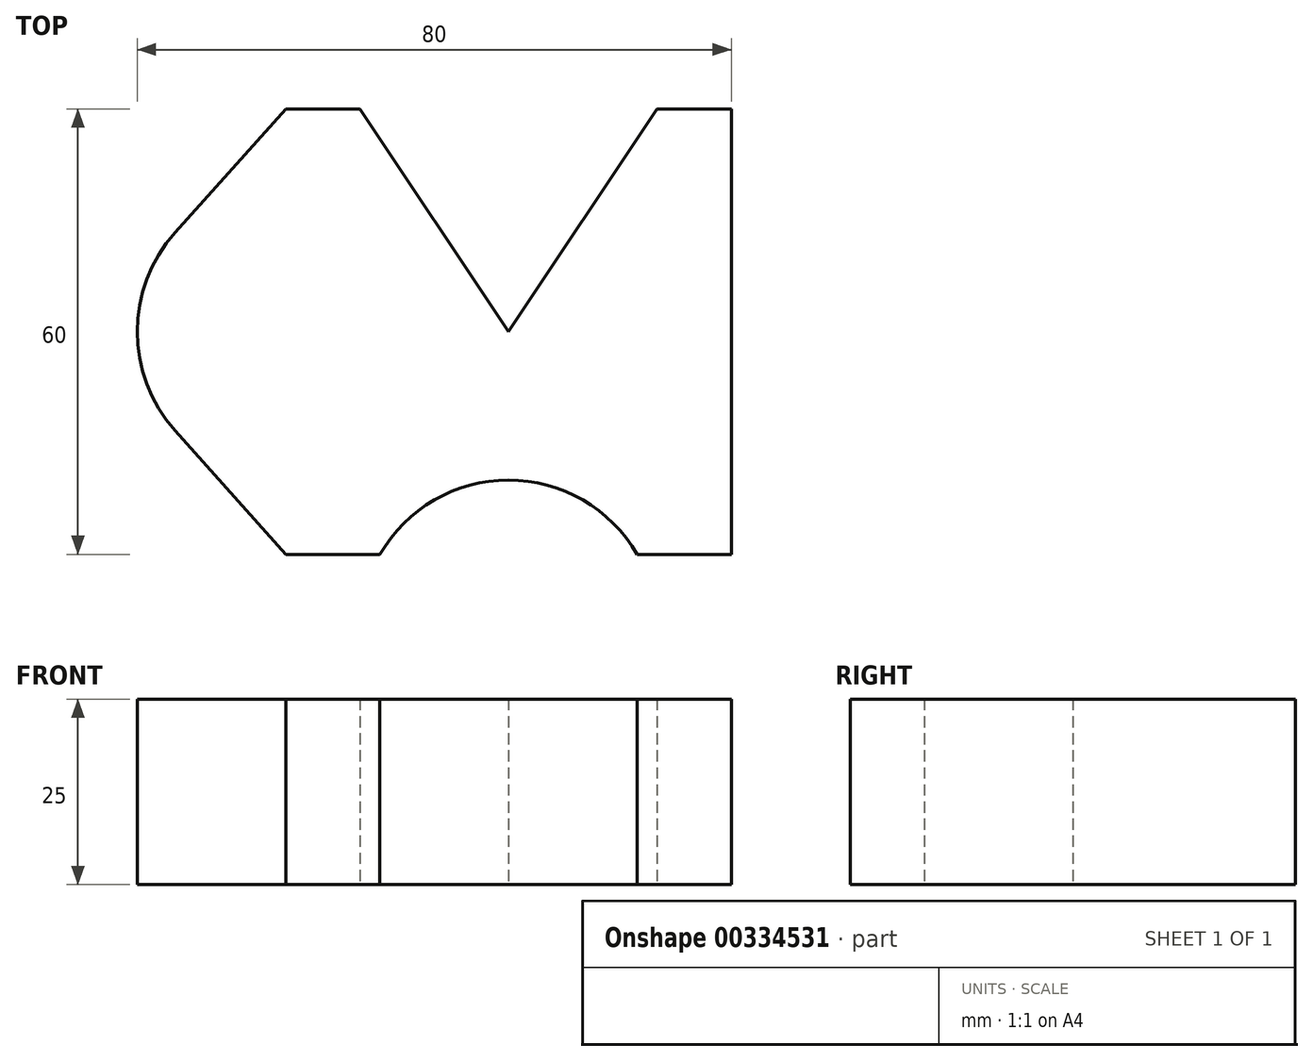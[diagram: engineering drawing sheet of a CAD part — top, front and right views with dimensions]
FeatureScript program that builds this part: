
annotation { "Feature Type Name" : "Feature", "Feature Type Description" : "" }
export const myFeature = defineFeature(function(context is Context, id is Id, definition is map)
    precondition{}
    {
        {
            var Q0;
            Q0=qCreatedBy(makeId("Top.planeOp"),FACE);
            var sketch = newSketch(context, id + "F0", { "sketchPlane" : qUnion([Q0])});
            skLineSegment(sketch, "E0", {"start": v(0, 0) * mm, "end": v(20, 30) * mm});
            skLineSegment(sketch, "E1", {"start": v(20, 30) * mm, "end": v(30, 30) * mm});
            skLineSegment(sketch, "E2", {"start": v(30, 30) * mm, "end": v(30, -30) * mm});
            skLineSegment(sketch, "E3", {"start": v(30, -30) * mm, "end": v(-19.9, -30) * mm});
            skCircle(sketch, "E4", {"center": v(-30, 0) * mm, "radius": 20 * mm});
            skCircle(sketch, "E5", {"center": v(0, -40) * mm, "radius": 20 * mm});
            skLineSegment(sketch, "E6", {"start": v(0, 0) * mm, "end": v(-20, 30) * mm});
            skLineSegment(sketch, "E7", {"start": v(-20, 30) * mm, "end": v(-30, 30) * mm});
            skLineSegment(sketch, "E8", {"start": v(-30, 30) * mm, "end": v(-44.9, 13.33) * mm});
            skLineSegment(sketch, "E9", {"start": v(-19.9, -30) * mm, "end": v(-30, -30) * mm});
            skLineSegment(sketch, "E10", {"start": v(-30, -30) * mm, "end": v(-44.9, -13.33) * mm});
            skSolve(sketch);
        }
        {
            var Q0;
            Q0=makeQuery(id+"F0.imprint","IMPRINT",FACE,{"disambiguationData":[TD([[makeQuery(id+"F0.imprint","IMPRINT",EDGE,{"derivedFrom":sQuery(id+"F0.wireOp",EDGE,"E0")}),-1.0]])]});
            var Q1;
            {var subQ0=sQuery(id+"F0.wireOp",EDGE,"E4");var subQ1=makeQuery(id+"F0.imprint","INTERSECT",VERTEX,{"derivedFrom":[subQ0,sQuery(id+"F0.wireOp",EDGE,"E8")]});Q1=makeQuery(id+"F0.imprint","IMPRINT",FACE,{"disambiguationData":[TD([[makeQuery(id+"F0.imprint","IMPRINT",EDGE,{"disambiguationData":[TD([[subQ1,-1.0]])],"derivedFrom":subQ0}),1.0]])]});}
            extrude(context, id + "F1", {"entities" : qUnion([Q0, Q1]), "depth" : 25 * mm});
        }
    });
